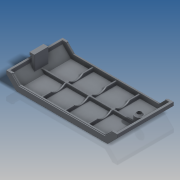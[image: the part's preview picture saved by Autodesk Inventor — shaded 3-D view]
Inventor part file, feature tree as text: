
AUTODESK INVENTOR PART (.ipt)
format: ipt  version: 2016 SP2 (Build 200236200, 236)  size: 565,248 bytes
history: native  units: in
note: dims shown in document units (in); Inventor stores cm internally (conversion verified against a paired STEP export)
features: extrude x8, sketch x7, revolve x3, pattern_linear x1, mirror x1, fillet x1
ambient origin geometry x8: Origin, YZ Plane, XZ Plane, XY Plane, X Axis, Y Axis, Z Axis, Center Point
bodies: Solid1 (feature_tree)
feature tree (21):
  sketch  "Sketch1"  dims[d0=2.4882in d1=1.2598in d2=0.0in]
  extrude  "Extrusion1"  Depth=1.2598in TaperAngle=0.0deg
  extrude  "Extrusion2"  Depth=0.0315in
  sketch  "Sketch3"  dims[d5=0.0787in d6=2.0472in]
  extrude  "Extrusion4"  Depth=2.0472in
  extrude  "Extrusion5"  Depth=0.1417in
  pattern_linear  "Rectangular Pattern1"  Spacing1=0.0157in  [1 undecoded]
  extrude  "Extrusion6"  Depth=0.0039in
  extrude  "Extrusion7"  Depth=0.0039in
  sketch  "Sketch6"  dims[d10=0.1417in]
  revolve  "Revolution1"  [1 undecoded]
  revolve  "Revolution2"  [1 undecoded]
  extrude  "Extrusion3"  Depth=0.0039in
  mirror  "Mirror1"
  revolve  "Revolution3"  [1 undecoded]
  extrude  "Extrusion8"  Depth=0.0039in
  fillet  "Fillet1"  Radius=0.4094in
  sketch  "Sketch2"  dims[d3=0.0472in d4=0.0315in]
  sketch  "Sketch4"  dims[d7=0.0787in d8=0.1417in]
  sketch  "Sketch5"  dims[d9=0.0157in]
  sketch  "Sketch7"  dims[d11=1.1654in d12=0.0in d13=0.0157in d14=0.0157in d15=0.0157in d16=0.0157in d17=0.0in d18=0.0787in d19=0.0315in d20=0.0945in d21=0.063in d22=0.4094in d23=0.0157in d24=0.0in d25=0.0315in d26=0.0in d27=1.1811in d29=0.5197in d30=0.063in d31=0.1102in d32=0.063in d33=0.0945in d34=0.1417in d35=0.315in d36=0.0in d37=0.189in d38=0.0945in d39=0.315in d40=0.0in d41=0.0315in d42=0.1417in d43=0.1575in d44=0.252in d45=90.0deg d46=90.0deg d47=0.252in d48=0.0157in d49=90.0deg d50=0.2205in d51=1.0079in d52=0.0945in d53=0.378in d54=0.4094in d55=0.0079in d56=0.0in d57=0.0039in]
note: 4 required parameter values undecoded (feature->parameter linkage not recoverable at this tier; creation-order binding heuristic only, values carry confidence <= 0.55)